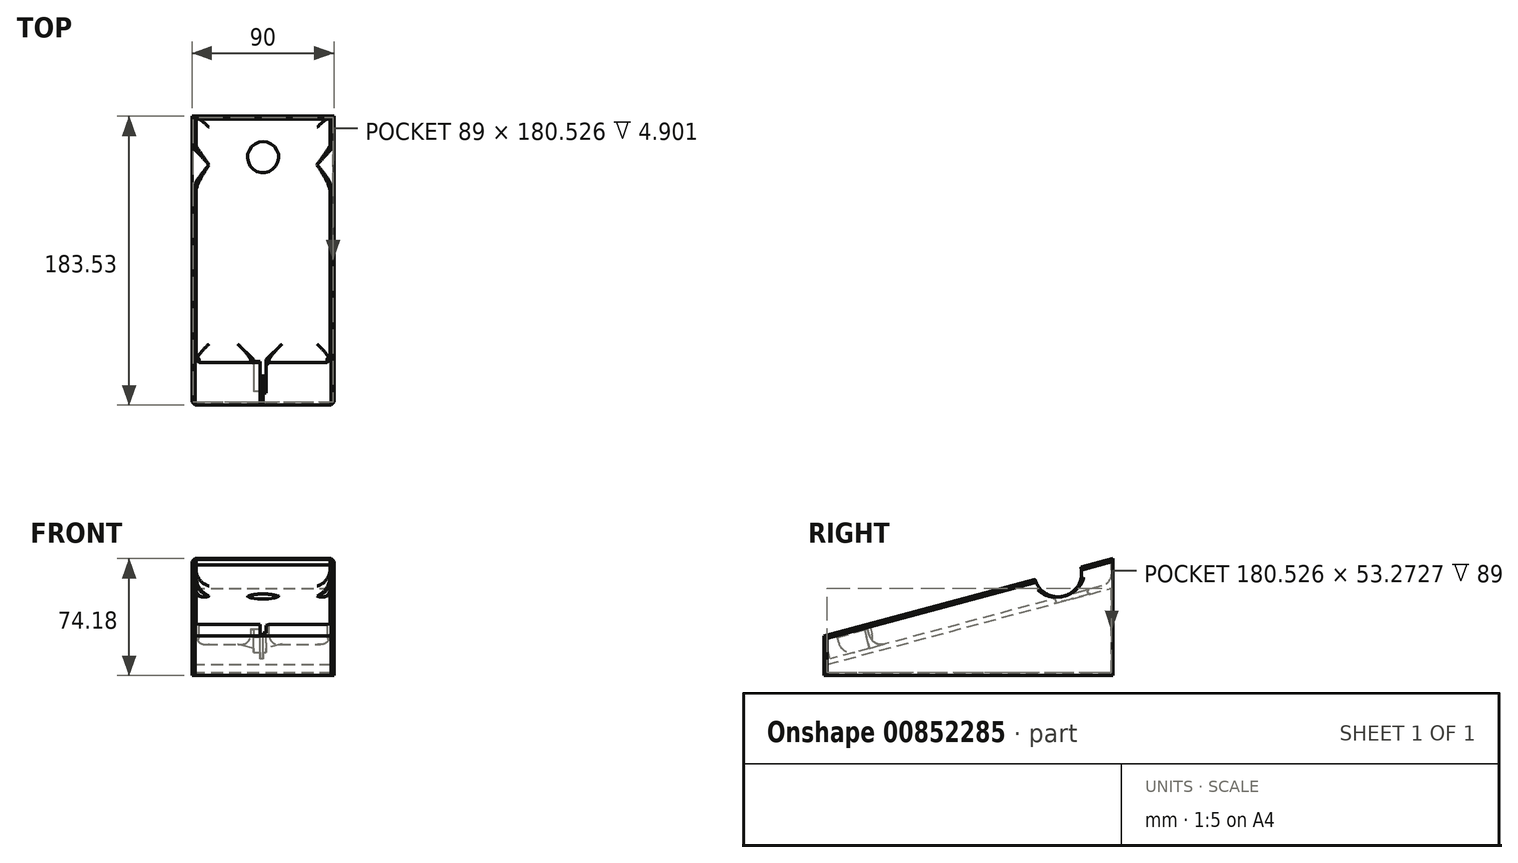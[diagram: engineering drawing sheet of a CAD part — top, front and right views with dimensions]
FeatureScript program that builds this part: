
annotation { "Feature Type Name" : "Feature", "Feature Type Description" : "" }
export const myFeature = defineFeature(function(context is Context, id is Id, definition is map)
    precondition{}
    {
        {
            var Q0;
            Q0=qCreatedBy(makeId("Right.planeOp"),FACE);
            var sketch = newSketch(context, id + "F0", { "sketchPlane" : qUnion([Q0])});
            skLineSegment(sketch, "E0.bottom", {"start": v(-87.42, 25) * mm, "end": v(96.1, 25) * mm});
            skLineSegment(sketch, "E0.top", {"start": v(-87.42, 0) * mm, "end": v(96.1, 0) * mm});
            skLineSegment(sketch, "E0.left", {"start": v(-87.42, 25) * mm, "end": v(-87.42, 0) * mm});
            skLineSegment(sketch, "E0.right", {"start": v(96.1, 25) * mm, "end": v(96.1, 0) * mm});
            skLineSegment(sketch, "E1", {"start": v(96.1, 25) * mm, "end": v(96.1, 74.18) * mm});
            skLineSegment(sketch, "E2", {"start": v(96.1, 74.18) * mm, "end": v(-87.42, 25) * mm});
            skLineSegment(sketch, "E3", {"start": v(95.1, 0) * mm, "end": v(95.1, 73.9) * mm});
            skLineSegment(sketch, "E4.bottom", {"start": v(-85.42, 2) * mm, "end": v(95.1, 2) * mm});
            skLineSegment(sketch, "E4.top", {"start": v(-85.42, 6.9) * mm, "end": v(95.1, 6.9) * mm});
            skLineSegment(sketch, "E4.left", {"start": v(-85.42, 2) * mm, "end": v(-85.42, 6.9) * mm});
            skLineSegment(sketch, "E4.right", {"start": v(95.1, 2) * mm, "end": v(95.1, 6.9) * mm});
            skLineSegment(sketch, "E5.top", {"start": v(70.1, 128.12) * mm, "end": v(80.1, 128.12) * mm});
            skLineSegment(sketch, "E5.left", {"start": v(70.1, 25) * mm, "end": v(70.1, 128.12) * mm});
            skLineSegment(sketch, "E5.right", {"start": v(80.1, 25) * mm, "end": v(80.1, 128.12) * mm});
            skLineSegment(sketch, "E6", {"start": v(-85.42, 6.9) * mm, "end": v(95.1, 55.27) * mm});
            skPoint(sketch, "E5.bottom.end.orphan", {"position": v(80.1, 6.9) * mm});
            skCircle(sketch, "E7", {"center": v(61.3, 64.85) * mm, "radius": 15 * mm});
            skSolve(sketch);
        }
        {
            var Q0;
            Q0=makeQuery(id+"F0.imprint","IMPRINT",FACE,{"disambiguationData":[TD([[makeQuery(id+"F0.imprint","IMPRINT",EDGE,{"derivedFrom":sQuery(id+"F0.wireOp",EDGE,"E0.bottom")}),1.0]])]});
            var Q1;
            Q1=makeQuery(id+"F0.imprint","IMPRINT",FACE,{"disambiguationData":[TD([[makeQuery(id+"F0.imprint","IMPRINT",EDGE,{"derivedFrom":sQuery(id+"F0.wireOp",EDGE,"E0.bottom")}),-1.0]])]});
            var Q2;
            {var subQ0=sQuery(id+"F0.wireOp",EDGE,"E1");Q2=makeQuery(id+"F0.imprint","IMPRINT",FACE,{"disambiguationData":[TD([[makeQuery(id+"F0.imprint","IMPRINT",EDGE,{"derivedFrom":subQ0}),1.0]])]});}
            var Q3;
            {var subQ5=sQuery(id+"F0.wireOp",EDGE,"E4.top");Q3=makeQuery(id+"F0.imprint","IMPRINT",FACE,{"disambiguationData":[TD([[makeQuery(id+"F0.imprint","IMPRINT",EDGE,{"derivedFrom":subQ5}),-1.0]])]});}
            var Q4;
            {var subQ5=sQuery(id+"F0.wireOp",EDGE,"E4.bottom");Q4=makeQuery(id+"F0.imprint","IMPRINT",FACE,{"disambiguationData":[TD([[makeQuery(id+"F0.imprint","IMPRINT",EDGE,{"derivedFrom":subQ5}),1.0]])]});}
            var Q5;
            {var subQ0=sQuery(id+"F0.wireOp",EDGE,"E0.right");Q5=makeQuery(id+"F0.imprint","IMPRINT",FACE,{"disambiguationData":[TD([[makeQuery(id+"F0.imprint","IMPRINT",EDGE,{"derivedFrom":subQ0}),-1.0]])]});}
            var Q6;
            {var subQ5=sQuery(id+"F0.wireOp",EDGE,"E5.bottom");Q6=makeQuery(id+"F0.imprint","IMPRINT",FACE,{"disambiguationData":[TD([[makeQuery(id+"F0.imprint","IMPRINT",EDGE,{"derivedFrom":subQ5}),1.0]])]});}
            var Q7;
            {var subQ0=sQuery(id+"F0.wireOp",EDGE,"E3");var subQ1=sQuery(id+"F0.wireOp",EDGE,"E2");var subQ2=makeQuery(id+"F0.imprint","INTERSECT",VERTEX,{"derivedFrom":[subQ1,subQ0]});Q7=makeQuery(id+"F0.imprint","IMPRINT",FACE,{"disambiguationData":[TD([[makeQuery(id+"F0.imprint","IMPRINT",EDGE,{"disambiguationData":[TD([[subQ2,-1.0]])],"derivedFrom":subQ1}),1.0]])]});}
            var Q8;
            {var subQ4=sQuery(id+"F0.wireOp",EDGE,"E0.left");Q8=makeQuery(id+"F0.imprint","IMPRINT",FACE,{"disambiguationData":[TD([[makeQuery(id+"F0.imprint","IMPRINT",EDGE,{"derivedFrom":subQ4}),1.0]])]});}
            var Q9;
            {var subQ0=sQuery(id+"F0.wireOp",EDGE,"E5.left");var subQ1=sQuery(id+"F0.wireOp",EDGE,"E2");var subQ2=makeQuery(id+"F0.imprint","INTERSECT",VERTEX,{"derivedFrom":[subQ1,subQ0]});Q9=makeQuery(id+"F0.imprint","IMPRINT",FACE,{"disambiguationData":[TD([[makeQuery(id+"F0.imprint","IMPRINT",EDGE,{"disambiguationData":[TD([[subQ2,-1.0]])],"derivedFrom":subQ1}),1.0]])]});}
            var Q10;
            {var subQ0=sQuery(id+"F0.wireOp",EDGE,"E6");var subQ3=sQuery(id+"F0.wireOp",EDGE,"E5.left");var subQ5=makeQuery(id+"F0.imprint","INTERSECT",VERTEX,{"derivedFrom":[subQ3,subQ0]});Q10=makeQuery(id+"F0.imprint","IMPRINT",FACE,{"disambiguationData":[TD([[makeQuery(id+"F0.imprint","IMPRINT",EDGE,{"disambiguationData":[TD([[subQ5,1.0]])],"derivedFrom":subQ3}),1.0]])]});}
            var Q11;
            {var subQ0=sQuery(id+"F0.wireOp",EDGE,"E5.right");var subQ1=sQuery(id+"F0.wireOp",EDGE,"E2");var subQ2=makeQuery(id+"F0.imprint","INTERSECT",VERTEX,{"derivedFrom":[subQ1,subQ0]});Q11=makeQuery(id+"F0.imprint","IMPRINT",FACE,{"disambiguationData":[TD([[makeQuery(id+"F0.imprint","IMPRINT",EDGE,{"disambiguationData":[TD([[subQ2,-1.0]])],"derivedFrom":subQ1}),1.0]])]});}
            var Q12;
            {var subQ1=sQuery(id+"F0.wireOp",EDGE,"E3");var subQ3=sQuery(id+"F0.wireOp",EDGE,"E6");var subQ4=makeQuery(id+"F0.imprint","INTERSECT",VERTEX,{"derivedFrom":[subQ1,subQ3]});Q12=makeQuery(id+"F0.imprint","IMPRINT",FACE,{"disambiguationData":[TD([[makeQuery(id+"F0.imprint","IMPRINT",EDGE,{"disambiguationData":[TD([[subQ4,1.0]])],"derivedFrom":subQ3}),-1.0]])]});}
            var Q13;
            {var subQ0=sQuery(id+"F0.wireOp",EDGE,"E5.left");var subQ1=sQuery(id+"F0.wireOp",EDGE,"E0.bottom");var subQ2=makeQuery(id+"F0.imprint","INTERSECT",VERTEX,{"derivedFrom":[subQ1,subQ0]});Q13=makeQuery(id+"F0.imprint","IMPRINT",FACE,{"disambiguationData":[TD([[makeQuery(id+"F0.imprint","IMPRINT",EDGE,{"disambiguationData":[TD([[subQ2,-1.0]])],"derivedFrom":subQ1}),1.0]])]});}
            var Q14;
            {var subQ0=sQuery(id+"F0.wireOp",EDGE,"E6");var subQ3=sQuery(id+"F0.wireOp",EDGE,"E5.left");var subQ4=makeQuery(id+"F0.imprint","INTERSECT",VERTEX,{"derivedFrom":[subQ3,subQ0]});Q14=makeQuery(id+"F0.imprint","IMPRINT",FACE,{"disambiguationData":[TD([[makeQuery(id+"F0.imprint","IMPRINT",EDGE,{"disambiguationData":[TD([[subQ4,-1.0]])],"derivedFrom":subQ3}),1.0]])]});}
            var Q15;
            {var subQ0=sQuery(id+"F0.wireOp",EDGE,"E7");var subQ1=sQuery(id+"F0.wireOp",EDGE,"E2");var subQ2=makeQuery(id+"F0.imprint","INTERSECT",VERTEX,{"disambiguationData":[OD(1.0)],"derivedFrom":[subQ1,subQ0]});Q15=makeQuery(id+"F0.imprint","IMPRINT",FACE,{"disambiguationData":[TD([[makeQuery(id+"F0.imprint","IMPRINT",EDGE,{"disambiguationData":[TD([[subQ2,-1.0]])],"derivedFrom":subQ1}),1.0]])]});}
            extrude(context, id + "F1", {"entities" : qUnion([Q0, Q1, Q2, Q3, Q4, Q5, Q6, Q7, Q8, Q9, Q10, Q11, Q12, Q13, Q14, Q15]), "endBound" : BoundingType.SYMMETRIC, "depth" : 90 * mm, "offsetDistance" : 25 * mm});
        }
        {
            var Q0;
            Q0=makeQuery(id+"F1.opExtrude","SWEPT_FACE",FACE,{"disambiguationData":[OSD([sQuery(id+"F0.wireOp",EDGE,"E2")])]});
            var sketch = newSketch(context, id + "F2", { "sketchPlane" : qUnion([Q0])});
            skLineSegment(sketch, "E8.bottom", {"start": v(-42.5, 110.03) * mm, "end": v(42.5, 110.03) * mm});
            skLineSegment(sketch, "E8.top", {"start": v(-42.5, -49.97) * mm, "end": v(42.5, -49.97) * mm});
            skLineSegment(sketch, "E8.left", {"start": v(-42.5, 110.03) * mm, "end": v(-42.5, -49.97) * mm});
            skLineSegment(sketch, "E8.right", {"start": v(42.5, 110.03) * mm, "end": v(42.5, -49.97) * mm});
            skLineSegment(sketch, "E9", {"start": v(-45, 2.35) * mm, "end": v(-42.5, 2.35) * mm, "construction": true});
            skLineSegment(sketch, "E10", {"start": v(42.5, 0) * mm, "end": v(45, 0) * mm, "construction": true});
            skLineSegment(sketch, "E11.bottom", {"start": v(0, -49.97) * mm, "end": v(6, -49.97) * mm});
            skLineSegment(sketch, "E11.top", {"start": v(0, -69.97) * mm, "end": v(6, -69.97) * mm});
            skLineSegment(sketch, "E11.left", {"start": v(0, -49.97) * mm, "end": v(0, -69.97) * mm});
            skLineSegment(sketch, "E11.right", {"start": v(6, -49.97) * mm, "end": v(6, -69.97) * mm});
            skLineSegment(sketch, "E12.MirrorCS", {"start": v(-6, -49.97) * mm, "end": v(-6, -69.97) * mm});
            skLineSegment(sketch, "E13.MirrorCS", {"start": v(0, -69.97) * mm, "end": v(-6, -69.97) * mm});
            skLineSegment(sketch, "E14.bottom", {"start": v(0, -69.97) * mm, "end": v(2, -69.97) * mm});
            skLineSegment(sketch, "E15.top", {"start": v(0, -87.25) * mm, "end": v(2, -87.25) * mm});
            skLineSegment(sketch, "E15.left", {"start": v(0, -69.97) * mm, "end": v(0, -87.25) * mm});
            skLineSegment(sketch, "E15.right", {"start": v(2, -69.97) * mm, "end": v(2, -87.25) * mm});
            skLineSegment(sketch, "E16.MirrorCS", {"start": v(-2, -69.97) * mm, "end": v(-2, -87.25) * mm});
            skLineSegment(sketch, "E17.MirrorCS", {"start": v(0, -87.25) * mm, "end": v(-2, -87.25) * mm});
            skLineSegment(sketch, "E18.bottom", {"start": v(2, -87.25) * mm, "end": v(-2, -87.25) * mm});
            skLineSegment(sketch, "E18.top", {"start": v(2, -49.97) * mm, "end": v(-2, -49.97) * mm});
            skLineSegment(sketch, "E18.left", {"start": v(2, -87.25) * mm, "end": v(2, -49.97) * mm});
            skLineSegment(sketch, "E18.right", {"start": v(-2, -87.25) * mm, "end": v(-2, -49.97) * mm});
            skSolve(sketch);
        }
        {
            var Q0;
            Q0=makeQuery(id+"F2.imprint","IMPRINT",FACE,{"disambiguationData":[TD([[makeQuery(id+"F2.imprint","IMPRINT",EDGE,{"derivedFrom":sQuery(id+"F2.wireOp",EDGE,"E8.bottom")}),-1.0]])]});
            var Q1;
            {var subQ0=sQuery(id+"F2.wireOp",EDGE,"E12.MirrorCS");Q1=makeQuery(id+"F2.imprint","IMPRINT",FACE,{"disambiguationData":[TD([[makeQuery(id+"F2.imprint","IMPRINT",EDGE,{"derivedFrom":subQ0}),1.0]])]});}
            var Q2;
            {var subQ0=sQuery(id+"F2.wireOp",EDGE,"E11.left");Q2=makeQuery(id+"F2.imprint","IMPRINT",FACE,{"disambiguationData":[TD([[makeQuery(id+"F2.imprint","IMPRINT",EDGE,{"derivedFrom":subQ0}),-1.0]])]});}
            var Q3;
            {var subQ0=sQuery(id+"F2.wireOp",EDGE,"E11.bottom");Q3=makeQuery(id+"F2.imprint","IMPRINT",FACE,{"disambiguationData":[TD([[makeQuery(id+"F2.imprint","IMPRINT",EDGE,{"derivedFrom":subQ0}),-1.0]])]});}
            var Q4;
            {var subQ0=sQuery(id+"F2.wireOp",EDGE,"E11.left");Q4=makeQuery(id+"F2.imprint","IMPRINT",FACE,{"disambiguationData":[TD([[makeQuery(id+"F2.imprint","IMPRINT",EDGE,{"derivedFrom":subQ0}),1.0]])]});}
            var Q5;
            {var subQ1=sQuery(id+"F2.wireOp",EDGE,"E13.MirrorCS");var subQ3=sQuery(id+"F2.wireOp",EDGE,"E18.right");var subQ4=makeQuery(id+"F2.imprint","INTERSECT",VERTEX,{"derivedFrom":[subQ1,subQ3]});Q5=makeQuery(id+"F2.imprint","IMPRINT",FACE,{"disambiguationData":[TD([[makeQuery(id+"F2.imprint","IMPRINT",EDGE,{"disambiguationData":[TD([[subQ4,1.0]])],"derivedFrom":subQ1}),1.0]])]});}
            var Q6;
            {var subQ0=sQuery(id+"F2.wireOp",EDGE,"E14.bottom");Q6=makeQuery(id+"F2.imprint","IMPRINT",FACE,{"disambiguationData":[TD([[makeQuery(id+"F2.imprint","IMPRINT",EDGE,{"derivedFrom":subQ0}),-1.0]])]});}
            var Q7;
            {var subQ0=sQuery(id+"F2.wireOp",EDGE,"E18.bottom");var subQ1=sQuery(id+"F2.wireOp",EDGE,"E15.left");var subQ2=makeQuery(id+"F2.imprint","INTERSECT",VERTEX,{"derivedFrom":[subQ1,subQ0]});Q7=makeQuery(id+"F2.imprint","IMPRINT",FACE,{"disambiguationData":[TD([[makeQuery(id+"F2.imprint","IMPRINT",EDGE,{"disambiguationData":[TD([[subQ2,-1.0]])],"derivedFrom":subQ0}),-1.0]])]});}
            var Q8;
            {var subQ0=sQuery(id+"F2.wireOp",EDGE,"E18.bottom");var subQ1=sQuery(id+"F2.wireOp",EDGE,"E15.left");var subQ2=makeQuery(id+"F2.imprint","INTERSECT",VERTEX,{"derivedFrom":[subQ1,subQ0]});Q8=makeQuery(id+"F2.imprint","IMPRINT",FACE,{"disambiguationData":[TD([[makeQuery(id+"F2.imprint","IMPRINT",EDGE,{"disambiguationData":[TD([[subQ2,1.0]])],"derivedFrom":subQ0}),-1.0]])]});}
            extrude(context, id + "F3", {"entities" : qUnion([Q0, Q1, Q2, Q3, Q4, Q5, Q6, Q7, Q8]), "operationType" : NewBodyOperationType.REMOVE, "oppositeDirection" : true, "depth" : 15 * mm, "offsetDistance" : 25 * mm});
        }
        {
            var Q0;
            {var subQ5=sQuery(id+"F0.wireOp",EDGE,"E4.top");Q0=makeQuery(id+"F0.imprint","IMPRINT",FACE,{"disambiguationData":[TD([[makeQuery(id+"F0.imprint","IMPRINT",EDGE,{"derivedFrom":subQ5}),-1.0]])]});}
            var Q1;
            {var subQ5=sQuery(id+"F0.wireOp",EDGE,"E4.bottom");Q1=makeQuery(id+"F0.imprint","IMPRINT",FACE,{"disambiguationData":[TD([[makeQuery(id+"F0.imprint","IMPRINT",EDGE,{"derivedFrom":subQ5}),1.0]])]});}
            var Q2;
            {var subQ0=sQuery(id+"F0.wireOp",EDGE,"E6");var subQ3=sQuery(id+"F0.wireOp",EDGE,"E5.left");var subQ5=makeQuery(id+"F0.imprint","INTERSECT",VERTEX,{"derivedFrom":[subQ3,subQ0]});Q2=makeQuery(id+"F0.imprint","IMPRINT",FACE,{"disambiguationData":[TD([[makeQuery(id+"F0.imprint","IMPRINT",EDGE,{"disambiguationData":[TD([[subQ5,1.0]])],"derivedFrom":subQ3}),1.0]])]});}
            var Q3;
            {var subQ1=sQuery(id+"F0.wireOp",EDGE,"E3");var subQ3=sQuery(id+"F0.wireOp",EDGE,"E6");var subQ4=makeQuery(id+"F0.imprint","INTERSECT",VERTEX,{"derivedFrom":[subQ1,subQ3]});Q3=makeQuery(id+"F0.imprint","IMPRINT",FACE,{"disambiguationData":[TD([[makeQuery(id+"F0.imprint","IMPRINT",EDGE,{"disambiguationData":[TD([[subQ4,1.0]])],"derivedFrom":subQ3}),-1.0]])]});}
            var Q4;
            {var subQ0=sQuery(id+"F0.wireOp",EDGE,"E5.left");var subQ1=sQuery(id+"F0.wireOp",EDGE,"E0.bottom");var subQ2=makeQuery(id+"F0.imprint","INTERSECT",VERTEX,{"derivedFrom":[subQ1,subQ0]});Q4=makeQuery(id+"F0.imprint","IMPRINT",FACE,{"disambiguationData":[TD([[makeQuery(id+"F0.imprint","IMPRINT",EDGE,{"disambiguationData":[TD([[subQ2,-1.0]])],"derivedFrom":subQ1}),1.0]])]});}
            var Q5;
            {var subQ0=sQuery(id+"F0.wireOp",EDGE,"E6");var subQ1=sQuery(id+"F0.wireOp",EDGE,"E0.bottom");var subQ2=makeQuery(id+"F0.imprint","INTERSECT",VERTEX,{"derivedFrom":[subQ1,subQ0]});Q5=makeQuery(id+"F0.imprint","IMPRINT",FACE,{"disambiguationData":[TD([[makeQuery(id+"F0.imprint","IMPRINT",EDGE,{"disambiguationData":[TD([[subQ2,-1.0]])],"derivedFrom":subQ1}),-1.0]])]});}
            var Q6;
            {var subQ5=sQuery(id+"F0.wireOp",EDGE,"E5.bottom");Q6=makeQuery(id+"F0.imprint","IMPRINT",FACE,{"disambiguationData":[TD([[makeQuery(id+"F0.imprint","IMPRINT",EDGE,{"derivedFrom":subQ5}),1.0]])]});}
            var Q7;
            {var subQ0=sQuery(id+"F0.wireOp",EDGE,"E5.right");var subQ1=sQuery(id+"F0.wireOp",EDGE,"E0.bottom");var subQ2=makeQuery(id+"F0.imprint","INTERSECT",VERTEX,{"derivedFrom":[subQ1,subQ0]});Q7=makeQuery(id+"F0.imprint","IMPRINT",FACE,{"disambiguationData":[TD([[makeQuery(id+"F0.imprint","IMPRINT",EDGE,{"disambiguationData":[TD([[subQ2,-1.0]])],"derivedFrom":subQ1}),-1.0]])]});}
            extrude(context, id + "F4", {"entities" : qUnion([Q0, Q1, Q2, Q3, Q4, Q5, Q6, Q7]), "operationType" : NewBodyOperationType.REMOVE, "endBound" : BoundingType.SYMMETRIC, "oppositeDirection" : true, "depth" : 89 * mm, "offsetDistance" : 25 * mm});
        }
        {
            var Q0;
            {var subQ0=sQuery(id+"F0.wireOp",EDGE,"E1");Q0=makeQuery(id+"F0.imprint","IMPRINT",FACE,{"disambiguationData":[TD([[makeQuery(id+"F0.imprint","IMPRINT",EDGE,{"derivedFrom":subQ0}),1.0]])]});}
            extrude(context, id + "F5", {"entities" : qUnion([Q0]), "operationType" : NewBodyOperationType.ADD, "endBound" : BoundingType.SYMMETRIC, "depth" : 90 * mm, "offsetDistance" : 25 * mm});
        }
        {
            var Q0;
            {var subQ0=sQuery(id+"F2.wireOp",EDGE,"E12.MirrorCS");Q0=makeQuery(id+"F2.imprint","IMPRINT",FACE,{"disambiguationData":[TD([[makeQuery(id+"F2.imprint","IMPRINT",EDGE,{"derivedFrom":subQ0}),1.0]])]});}
            var Q1;
            {var subQ0=sQuery(id+"F2.wireOp",EDGE,"E11.bottom");Q1=makeQuery(id+"F2.imprint","IMPRINT",FACE,{"disambiguationData":[TD([[makeQuery(id+"F2.imprint","IMPRINT",EDGE,{"derivedFrom":subQ0}),-1.0]])]});}
            extrude(context, id + "F6", {"entities" : qUnion([Q0, Q1]), "operationType" : NewBodyOperationType.ADD, "depth" : 0 * mm, "offsetDistance" : 25 * mm, "hasSecondDirection" : true, "secondDirectionOppositeDirection" : true, "secondDirectionDepth" : 3 * mm});
        }
        {
            var Q0;
            {var subQ5=sQuery(id+"F0.wireOp",EDGE,"E5.top");Q0=makeQuery(id+"F0.imprint","IMPRINT",FACE,{"disambiguationData":[TD([[makeQuery(id+"F0.imprint","IMPRINT",EDGE,{"derivedFrom":subQ5}),-1.0]])]});}
            var Q1;
            {var subQ0=sQuery(id+"F0.wireOp",EDGE,"E5.right");var subQ1=sQuery(id+"F0.wireOp",EDGE,"E2");var subQ2=makeQuery(id+"F0.imprint","INTERSECT",VERTEX,{"derivedFrom":[subQ1,subQ0]});Q1=makeQuery(id+"F0.imprint","IMPRINT",FACE,{"disambiguationData":[TD([[makeQuery(id+"F0.imprint","IMPRINT",EDGE,{"disambiguationData":[TD([[subQ2,-1.0]])],"derivedFrom":subQ1}),1.0]])]});}
            var Q2;
            {var subQ0=sQuery(id+"F0.wireOp",EDGE,"E5.left");var subQ1=sQuery(id+"F0.wireOp",EDGE,"E0.bottom");var subQ2=makeQuery(id+"F0.imprint","INTERSECT",VERTEX,{"derivedFrom":[subQ1,subQ0]});Q2=makeQuery(id+"F0.imprint","IMPRINT",FACE,{"disambiguationData":[TD([[makeQuery(id+"F0.imprint","IMPRINT",EDGE,{"disambiguationData":[TD([[subQ2,-1.0]])],"derivedFrom":subQ1}),1.0]])]});}
            var Q3;
            Q3=sQuery(id+"F0.wireOp",EDGE,"E5.left");
            revolve(context, id + "F7", {"operationType" : NewBodyOperationType.REMOVE, "surfaceOperationType" : NewSurfaceOperationType.NEW, "entities" : qUnion([Q0, Q1, Q2]), "axis" : qUnion([Q3]), "revolveType" : RevolveType.FULL, "oppositeDirection" : true});
        }
        {
            var Q0;
            {var subQ0=sQuery(id+"F0.wireOp",EDGE,"E2");var subQ1=sQuery(id+"F0.wireOp",EDGE,"E0.left");Q0=makeQuery(id+"F3.boolean.opBoolean","SPLIT",EDGE,{"disambiguationData":[TD([makeQuery(id+"F3.opExtrude","SWEPT_FACE",FACE,{"disambiguationData":[OSD([sQuery(id+"F2.wireOp",EDGE,"E18.right")])]})])],"derivedFrom":makeQuery(id+"F1.opExtrude","SWEPT_EDGE",EDGE,{"disambiguationData":[OSD([sQuery(id+"F0.wireOp",EDGE,"E0.bottom"),subQ1,subQ0])]})});}
            var Q1;
            {var subQ0=sQuery(id+"F0.wireOp",EDGE,"E2");var subQ1=sQuery(id+"F0.wireOp",EDGE,"E0.left");Q1=makeQuery(id+"F3.boolean.opBoolean","SPLIT",EDGE,{"disambiguationData":[TD([makeQuery(id+"F3.opExtrude","SWEPT_FACE",FACE,{"disambiguationData":[OSD([sQuery(id+"F2.wireOp",EDGE,"E18.left")])]})])],"derivedFrom":makeQuery(id+"F1.opExtrude","SWEPT_EDGE",EDGE,{"disambiguationData":[OSD([sQuery(id+"F0.wireOp",EDGE,"E0.bottom"),subQ1,subQ0])]})});}
            var Q2;
            Q2=makeQuery(id+"F1.opExtrude","CAP_EDGE",EDGE,{"disambiguationData":[OSD([sQuery(id+"F0.wireOp",EDGE,"E0.left")])],"isStart":true});
            var Q3;
            Q3=makeQuery(id+"F1.opExtrude","CAP_EDGE",EDGE,{"disambiguationData":[OSD([sQuery(id+"F0.wireOp",EDGE,"E0.left")])],"isStart":false});
            var Q4;
            Q4=makeQuery(id+"F1.opExtrude","CAP_EDGE",EDGE,{"disambiguationData":[OSD([sQuery(id+"F0.wireOp",EDGE,"E2")])],"isStart":false});
            var Q5;
            Q5=makeQuery(id+"F1.opExtrude","CAP_EDGE",EDGE,{"disambiguationData":[OSD([sQuery(id+"F0.wireOp",EDGE,"E2")])],"isStart":true});
            var Q6;
            Q6=makeQuery(id+"F3.boolean.opBoolean","INTERSECT",EDGE,{"derivedFrom":[makeQuery(id+"F1.opExtrude","SWEPT_FACE",FACE,{"disambiguationData":[OSD([sQuery(id+"F0.wireOp",EDGE,"E0.left")])]}),makeQuery(id+"F3.opExtrude","SWEPT_FACE",FACE,{"disambiguationData":[OSD([sQuery(id+"F2.wireOp",EDGE,"E18.right")])]})]});
            var Q7;
            Q7=makeQuery(id+"F3.boolean.opBoolean","INTERSECT",EDGE,{"derivedFrom":[makeQuery(id+"F1.opExtrude","SWEPT_FACE",FACE,{"disambiguationData":[OSD([sQuery(id+"F0.wireOp",EDGE,"E0.left")])]}),makeQuery(id+"F3.opExtrude","CAP_FACE",FACE,{"disambiguationData":[OSD([sQuery(id+"F2.wireOp",EDGE,"E8.bottom"),sQuery(id+"F2.wireOp",EDGE,"E8.top"),sQuery(id+"F2.wireOp",EDGE,"E8.left"),sQuery(id+"F2.wireOp",EDGE,"E8.right"),sQuery(id+"F2.wireOp",EDGE,"E11.top"),sQuery(id+"F2.wireOp",EDGE,"E11.right"),sQuery(id+"F2.wireOp",EDGE,"E12.MirrorCS"),sQuery(id+"F2.wireOp",EDGE,"E13.MirrorCS"),sQuery(id+"F2.wireOp",EDGE,"E18.bottom"),sQuery(id+"F2.wireOp",EDGE,"E18.left"),sQuery(id+"F2.wireOp",EDGE,"E18.right")])],"isStart":false})]});
            var Q8;
            Q8=makeQuery(id+"F3.boolean.opBoolean","INTERSECT",EDGE,{"derivedFrom":[makeQuery(id+"F1.opExtrude","SWEPT_FACE",FACE,{"disambiguationData":[OSD([sQuery(id+"F0.wireOp",EDGE,"E0.left")])]}),makeQuery(id+"F3.opExtrude","SWEPT_FACE",FACE,{"disambiguationData":[OSD([sQuery(id+"F2.wireOp",EDGE,"E18.left")])]})]});
            var Q9;
            Q9=makeQuery(id+"F3.boolean.opBoolean","COPY",EDGE,{"derivedFrom":makeQuery(id+"F3.opExtrude","SWEPT_EDGE",EDGE,{"disambiguationData":[OSD([sQuery(id+"F2.wireOp",EDGE,"E8.top"),sQuery(id+"F2.wireOp",EDGE,"E11.bottom"),sQuery(id+"F2.wireOp",EDGE,"E11.right")])]})});
            var Q10;
            Q10=makeQuery(id+"F3.boolean.opBoolean","COPY",EDGE,{"derivedFrom":makeQuery(id+"F3.opExtrude","SWEPT_EDGE",EDGE,{"disambiguationData":[OSD([sQuery(id+"F2.wireOp",EDGE,"E8.top"),sQuery(id+"F2.wireOp",EDGE,"E12.MirrorCS")])]})});
            chamfer(context, id + "F8", {"entities" : qUnion([Q0, Q1, Q2, Q3, Q4, Q5, Q6, Q7, Q8, Q9, Q10]), "width" : 1.9 * mm, "tangentPropagation" : true});
        }
        {
            var Q0;
            Q0=makeQuery(id+"F3.boolean.opBoolean","COPY",EDGE,{"derivedFrom":makeQuery(id+"F3.opExtrude","CAP_EDGE",EDGE,{"disambiguationData":[OSD([sQuery(id+"F2.wireOp",EDGE,"E8.right")])],"isStart":false})});
            var Q1;
            {var subQ0=sQuery(id+"F2.wireOp",EDGE,"E8.top");Q1=makeQuery(id+"F3.boolean.opBoolean","COPY",EDGE,{"derivedFrom":makeQuery(id+"F3.opExtrude","CAP_EDGE",EDGE,{"disambiguationData":[OSD([subQ0]),TDD([makeQuery(id+"F2.imprint","IMPRINT",EDGE,{"disambiguationData":[TD([[makeQuery(id+"F2.imprint","INTERSECT",VERTEX,{"derivedFrom":[subQ0,sQuery(id+"F2.wireOp",EDGE,"E8.right")]}),1.0]])],"derivedFrom":subQ0})])],"isStart":false})});}
            var Q2;
            {var subQ0=sQuery(id+"F2.wireOp",EDGE,"E8.top");Q2=makeQuery(id+"F3.boolean.opBoolean","COPY",EDGE,{"derivedFrom":makeQuery(id+"F3.opExtrude","CAP_EDGE",EDGE,{"disambiguationData":[OSD([subQ0]),TDD([makeQuery(id+"F2.imprint","IMPRINT",EDGE,{"disambiguationData":[TD([[makeQuery(id+"F2.imprint","INTERSECT",VERTEX,{"derivedFrom":[subQ0,sQuery(id+"F2.wireOp",EDGE,"E8.left")]}),-1.0]])],"derivedFrom":subQ0})])],"isStart":false})});}
            var Q3;
            Q3=makeQuery(id+"F3.boolean.opBoolean","COPY",EDGE,{"derivedFrom":makeQuery(id+"F3.opExtrude","CAP_EDGE",EDGE,{"disambiguationData":[OSD([sQuery(id+"F2.wireOp",EDGE,"E8.left")])],"isStart":false})});
            var Q4;
            Q4=makeQuery(id+"F5.boolean.opBoolean","INTERSECT",EDGE,{"derivedFrom":[makeQuery(id+"F3.boolean.opBoolean","COPY",FACE,{"derivedFrom":makeQuery(id+"F3.opExtrude","CAP_FACE",FACE,{"disambiguationData":[OSD([sQuery(id+"F2.wireOp",EDGE,"E8.bottom"),sQuery(id+"F2.wireOp",EDGE,"E8.top"),sQuery(id+"F2.wireOp",EDGE,"E8.left"),sQuery(id+"F2.wireOp",EDGE,"E8.right"),sQuery(id+"F2.wireOp",EDGE,"E11.top"),sQuery(id+"F2.wireOp",EDGE,"E11.right"),sQuery(id+"F2.wireOp",EDGE,"E12.MirrorCS"),sQuery(id+"F2.wireOp",EDGE,"E13.MirrorCS"),sQuery(id+"F2.wireOp",EDGE,"E18.bottom"),sQuery(id+"F2.wireOp",EDGE,"E18.left"),sQuery(id+"F2.wireOp",EDGE,"E18.right")])],"isStart":false})}),makeQuery(id+"F5.opExtrude","SWEPT_FACE",FACE,{"disambiguationData":[OSD([sQuery(id+"F0.wireOp",EDGE,"E3")])]})]});
            var Q5;
            Q5=makeQuery(id+"F3.boolean.opBoolean","COPY",EDGE,{"derivedFrom":makeQuery(id+"F3.opExtrude","CAP_EDGE",EDGE,{"disambiguationData":[OSD([sQuery(id+"F2.wireOp",EDGE,"E11.top")])],"isStart":false})});
            var Q6;
            Q6=makeQuery(id+"F3.boolean.opBoolean","COPY",EDGE,{"derivedFrom":makeQuery(id+"F3.opExtrude","CAP_EDGE",EDGE,{"disambiguationData":[OSD([sQuery(id+"F2.wireOp",EDGE,"E13.MirrorCS")])],"isStart":false})});
            fillet(context, id + "F9", {"entities" : qUnion([Q0, Q1, Q2, Q3, Q4, Q5, Q6]), "radius" : 8.2 * mm, "tangentPropagation" : true, "allowEdgeOverflow" : false});
        }
        {
            var Q0;
            {var subQ0=sQuery(id+"F0.wireOp",EDGE,"E7");var subQ1=sQuery(id+"F0.wireOp",EDGE,"E2");var subQ2=makeQuery(id+"F0.imprint","INTERSECT",VERTEX,{"disambiguationData":[OD(0.0)],"derivedFrom":[subQ1,subQ0]});Q0=makeQuery(id+"F0.imprint","IMPRINT",FACE,{"disambiguationData":[TD([[makeQuery(id+"F0.imprint","IMPRINT",EDGE,{"disambiguationData":[TD([[subQ2,1.0]])],"derivedFrom":subQ1}),-1.0]])]});}
            var Q1;
            {var subQ0=sQuery(id+"F0.wireOp",EDGE,"E7");var subQ1=sQuery(id+"F0.wireOp",EDGE,"E2");var subQ2=makeQuery(id+"F0.imprint","INTERSECT",VERTEX,{"disambiguationData":[OD(1.0)],"derivedFrom":[subQ1,subQ0]});Q1=makeQuery(id+"F0.imprint","IMPRINT",FACE,{"disambiguationData":[TD([[makeQuery(id+"F0.imprint","IMPRINT",EDGE,{"disambiguationData":[TD([[subQ2,-1.0]])],"derivedFrom":subQ1}),-1.0]])]});}
            var Q2;
            {var subQ0=sQuery(id+"F0.wireOp",EDGE,"E7");var subQ1=sQuery(id+"F0.wireOp",EDGE,"E2");var subQ2=makeQuery(id+"F0.imprint","INTERSECT",VERTEX,{"disambiguationData":[OD(1.0)],"derivedFrom":[subQ1,subQ0]});Q2=makeQuery(id+"F0.imprint","IMPRINT",FACE,{"disambiguationData":[TD([[makeQuery(id+"F0.imprint","IMPRINT",EDGE,{"disambiguationData":[TD([[subQ2,-1.0]])],"derivedFrom":subQ1}),1.0]])]});}
            var Q3;
            {var subQ0=sQuery(id+"F0.wireOp",EDGE,"E7");var subQ1=sQuery(id+"F0.wireOp",EDGE,"E2");var subQ2=makeQuery(id+"F0.imprint","INTERSECT",VERTEX,{"disambiguationData":[OD(0.0)],"derivedFrom":[subQ1,subQ0]});Q3=makeQuery(id+"F0.imprint","IMPRINT",FACE,{"disambiguationData":[TD([[makeQuery(id+"F0.imprint","IMPRINT",EDGE,{"disambiguationData":[TD([[subQ2,1.0]])],"derivedFrom":subQ1}),1.0]])]});}
            extrude(context, id + "F10", {"entities" : qUnion([Q0, Q1, Q2, Q3]), "operationType" : NewBodyOperationType.REMOVE, "endBound" : BoundingType.SYMMETRIC, "depth" : 125 * mm, "offsetDistance" : 25 * mm});
        }
        {
            var Q0;
            Q0=makeQuery(id+"F7.boolean.opBoolean","COPY",FACE,{"derivedFrom":makeQuery(id+"F7.opRevolve","SWEPT_FACE",FACE,{"disambiguationData":[OSD([sQuery(id+"F0.wireOp",EDGE,"E5.right")])]})});
            var Q1;
            {var subQ1=sQuery(id+"F2.wireOp",EDGE,"E8.left");Q1=makeQuery(id+"F10.boolean.opBoolean","COPY",FACE,{"disambiguationData":[TD([makeQuery(id+"F3.boolean.opBoolean","COPY",FACE,{"derivedFrom":makeQuery(id+"F3.opExtrude","SWEPT_FACE",FACE,{"disambiguationData":[OSD([subQ1])]})})])],"derivedFrom":makeQuery(id+"F10.opExtrude","SWEPT_FACE",FACE,{"disambiguationData":[OSD([sQuery(id+"F0.wireOp",EDGE,"E7")])]})});}
            var Q2;
            {var subQ0=sQuery(id+"F2.wireOp",EDGE,"E8.right");Q2=makeQuery(id+"F10.boolean.opBoolean","COPY",FACE,{"disambiguationData":[TD([makeQuery(id+"F3.boolean.opBoolean","COPY",FACE,{"derivedFrom":makeQuery(id+"F3.opExtrude","SWEPT_FACE",FACE,{"disambiguationData":[OSD([subQ0])]})})])],"derivedFrom":makeQuery(id+"F10.opExtrude","SWEPT_FACE",FACE,{"disambiguationData":[OSD([sQuery(id+"F0.wireOp",EDGE,"E7")])]})});}
            fillet(context, id + "F11", {"entities" : qUnion([Q0, Q1, Q2]), "radius" : 1.5 * mm, "tangentPropagation" : true, "allowEdgeOverflow" : false});
        }
    });
